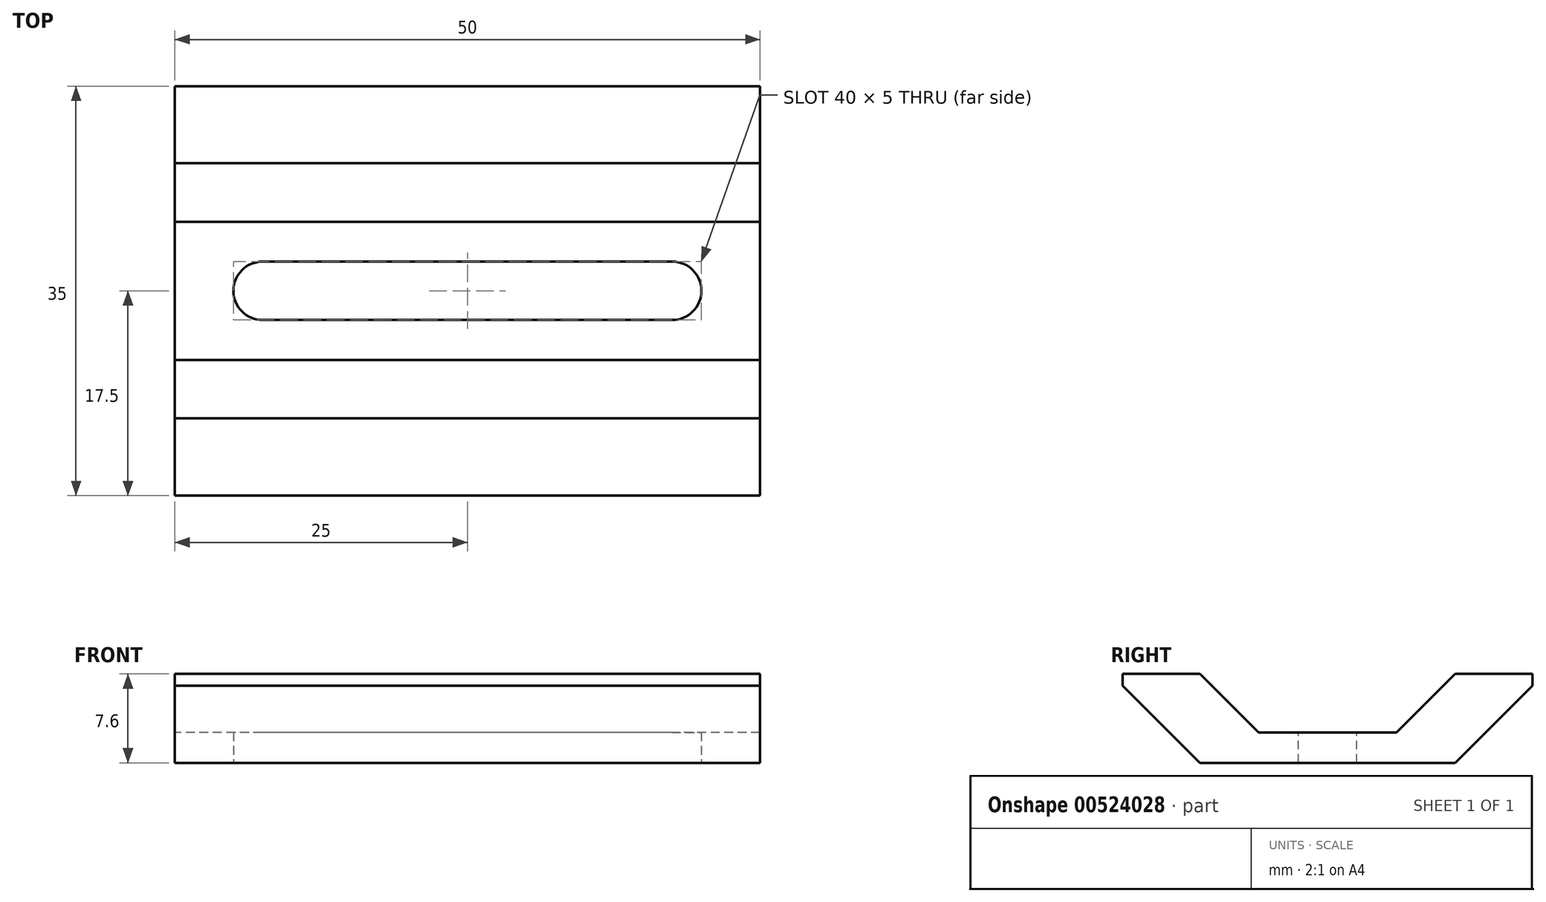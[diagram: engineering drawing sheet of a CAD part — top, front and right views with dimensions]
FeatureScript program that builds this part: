
annotation { "Feature Type Name" : "Feature", "Feature Type Description" : "" }
export const myFeature = defineFeature(function(context is Context, id is Id, definition is map)
    precondition{}
    {
        {
            var Q0;
            Q0=qCreatedBy(makeId("Top.planeOp"),FACE);
            var sketch = newSketch(context, id + "F0", { "sketchPlane" : qUnion([Q0])});
            skLineSegment(sketch, "E0.bottom", {"start": v(25, -17.5) * mm, "end": v(-25, -17.5) * mm});
            skLineSegment(sketch, "E0.top", {"start": v(25, 17.5) * mm, "end": v(-25, 17.5) * mm});
            skLineSegment(sketch, "E0.left", {"start": v(25, -17.5) * mm, "end": v(25, 17.5) * mm});
            skLineSegment(sketch, "E0.right", {"start": v(-25, -17.5) * mm, "end": v(-25, 17.5) * mm});
            skPoint(sketch, "E0.middle", {"position": v(0, 0) * mm});
            skSolve(sketch);
        }
        {
            var Q0;
            Q0=makeQuery(id+"F0.imprint","IMPRINT",FACE,{"disambiguationData":[TD([[makeQuery(id+"F0.imprint","IMPRINT",EDGE,{"derivedFrom":sQuery(id+"F0.wireOp",EDGE,"E0.bottom")}),-1.0]])]});
            extrude(context, id + "F1", {"entities" : qUnion([Q0]), "depth" : 7.6 * mm, "offsetDistance" : 25 * mm});
        }
        {
            var Q0;
            Q0=makeQuery(id+"F1.opExtrude","CAP_FACE",FACE,{"disambiguationData":[OSD([sQuery(id+"F0.wireOp",EDGE,"E0.bottom"),sQuery(id+"F0.wireOp",EDGE,"E0.top"),sQuery(id+"F0.wireOp",EDGE,"E0.left"),sQuery(id+"F0.wireOp",EDGE,"E0.right")])],"isStart":false});
            var sketch = newSketch(context, id + "F2", { "sketchPlane" : qUnion([Q0])});
            skLineSegment(sketch, "E1.bottom", {"start": v(25, -12.5) * mm, "end": v(-25, -12.5) * mm});
            skLineSegment(sketch, "E1.top", {"start": v(25, 12.5) * mm, "end": v(-25, 12.5) * mm});
            skLineSegment(sketch, "E1.left", {"start": v(25, -12.5) * mm, "end": v(25, 12.5) * mm});
            skLineSegment(sketch, "E1.right", {"start": v(-25, -12.5) * mm, "end": v(-25, 12.5) * mm});
            skPoint(sketch, "E1.middle", {"position": v(0, 0) * mm});
            skSolve(sketch);
        }
        {
            var Q0;
            Q0=makeQuery(id+"F2.imprint","IMPRINT",FACE,{"disambiguationData":[TD([[makeQuery(id+"F2.imprint","IMPRINT",EDGE,{"derivedFrom":sQuery(id+"F2.wireOp",EDGE,"E1.bottom")}),-1.0]])]});
            extrude(context, id + "F3", {"entities" : qUnion([Q0]), "operationType" : NewBodyOperationType.REMOVE, "oppositeDirection" : true, "depth" : 5 * mm, "offsetDistance" : 25 * mm});
        }
        {
            var Q0;
            Q0=makeQuery(id+"F1.opExtrude","CAP_EDGE",EDGE,{"disambiguationData":[OSD([sQuery(id+"F0.wireOp",EDGE,"E0.top")])],"isStart":true});
            var Q1;
            Q1=makeQuery(id+"F1.opExtrude","CAP_EDGE",EDGE,{"disambiguationData":[OSD([sQuery(id+"F0.wireOp",EDGE,"E0.bottom")])],"isStart":true});
            var Q2;
            Q2=makeQuery(id+"F3.boolean.opBoolean","COPY",EDGE,{"derivedFrom":makeQuery(id+"F3.opExtrude","CAP_EDGE",EDGE,{"disambiguationData":[OSD([sQuery(id+"F2.wireOp",EDGE,"E1.top")])],"isStart":false})});
            var Q3;
            Q3=makeQuery(id+"F3.boolean.opBoolean","COPY",EDGE,{"derivedFrom":makeQuery(id+"F3.opExtrude","CAP_EDGE",EDGE,{"disambiguationData":[OSD([sQuery(id+"F2.wireOp",EDGE,"E1.bottom")])],"isStart":false})});
            chamfer(context, id + "F4", {"entities" : qUnion([Q0, Q1, Q2, Q3]), "width" : 6.6 * mm, "tangentPropagation" : true});
        }
        {
            var Q0;
            Q0=makeQuery(id+"F3.boolean.opBoolean","COPY",FACE,{"derivedFrom":makeQuery(id+"F3.opExtrude","CAP_FACE",FACE,{"disambiguationData":[OSD([sQuery(id+"F2.wireOp",EDGE,"E1.bottom"),sQuery(id+"F2.wireOp",EDGE,"E1.top"),sQuery(id+"F2.wireOp",EDGE,"E1.left"),sQuery(id+"F2.wireOp",EDGE,"E1.right")])],"isStart":false})});
            var sketch = newSketch(context, id + "F5", { "sketchPlane" : qUnion([Q0])});
            skLineSegment(sketch, "E2.bottom", {"start": v(20, -2.5) * mm, "end": v(-20, -2.5) * mm});
            skLineSegment(sketch, "E2.top", {"start": v(20, 2.5) * mm, "end": v(-20, 2.5) * mm});
            skLineSegment(sketch, "E2.left", {"start": v(20, -2.5) * mm, "end": v(20, 2.5) * mm});
            skLineSegment(sketch, "E2.right", {"start": v(-20, -2.5) * mm, "end": v(-20, 2.5) * mm});
            skPoint(sketch, "E2.middle", {"position": v(0, 0) * mm});
            skSolve(sketch);
        }
        {
            var Q0;
            Q0=makeQuery(id+"F5.imprint","IMPRINT",FACE,{"disambiguationData":[TD([[makeQuery(id+"F5.imprint","IMPRINT",EDGE,{"derivedFrom":sQuery(id+"F5.wireOp",EDGE,"E2.bottom")}),-1.0]])]});
            extrude(context, id + "F6", {"entities" : qUnion([Q0]), "operationType" : NewBodyOperationType.REMOVE, "endBound" : BoundingType.UP_TO_NEXT, "oppositeDirection" : true, "depth" : 25 * mm, "offsetDistance" : 25 * mm});
        }
        {
            var Q0;
            Q0=makeQuery(id+"F6.boolean.opBoolean","COPY",EDGE,{"derivedFrom":makeQuery(id+"F6.opExtrude","SWEPT_EDGE",EDGE,{"disambiguationData":[OSD([sQuery(id+"F5.wireOp",EDGE,"E2.bottom"),sQuery(id+"F5.wireOp",EDGE,"E2.right")])]})});
            var Q1;
            Q1=makeQuery(id+"F6.boolean.opBoolean","COPY",EDGE,{"derivedFrom":makeQuery(id+"F6.opExtrude","SWEPT_EDGE",EDGE,{"disambiguationData":[OSD([sQuery(id+"F5.wireOp",EDGE,"E2.top"),sQuery(id+"F5.wireOp",EDGE,"E2.right")])]})});
            var Q2;
            Q2=makeQuery(id+"F6.boolean.opBoolean","COPY",EDGE,{"derivedFrom":makeQuery(id+"F6.opExtrude","SWEPT_EDGE",EDGE,{"disambiguationData":[OSD([sQuery(id+"F5.wireOp",EDGE,"E2.top"),sQuery(id+"F5.wireOp",EDGE,"E2.left")])]})});
            var Q3;
            Q3=makeQuery(id+"F6.boolean.opBoolean","COPY",EDGE,{"derivedFrom":makeQuery(id+"F6.opExtrude","SWEPT_EDGE",EDGE,{"disambiguationData":[OSD([sQuery(id+"F5.wireOp",EDGE,"E2.bottom"),sQuery(id+"F5.wireOp",EDGE,"E2.left")])]})});
            fillet(context, id + "F7", {"entities" : qUnion([Q0, Q1, Q2, Q3]), "radius" : 2.5 * mm, "tangentPropagation" : true, "allowEdgeOverflow" : false});
        }
    });
